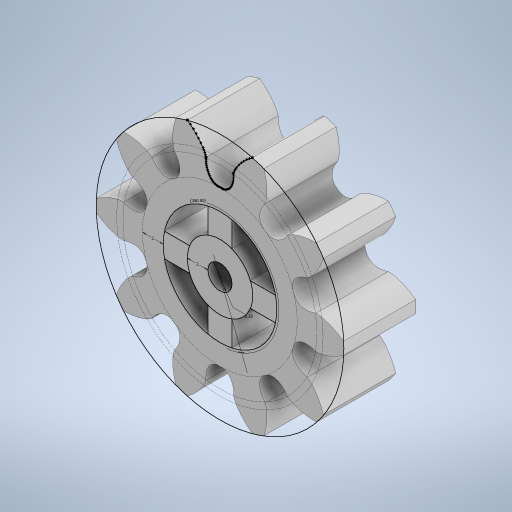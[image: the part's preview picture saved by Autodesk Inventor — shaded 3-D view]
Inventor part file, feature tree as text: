
AUTODESK INVENTOR PART (.ipt)
format: ipt  version: 2023 (Build 270158000, 158)  size: 391,680 bytes
history: native  units: mm
features: extrude x3, sketch x1, pattern_circular x1
ambient origin geometry x8: Origin, YZ Plane, XZ Plane, XY Plane, X Axis, Y Axis, Z Axis, Center Point
bodies: Solid1 (feature_tree)
feature tree (5):
  sketch  "Sketch1"  dims[d0=7.0mm d1=0.0mm d2=2.33mm d3=2.0mm d4=2.0mm d5=40.0mm d7=360.0deg d9=0.0mm d10=0.0mm d11=0.0mm d12=0.0mm d13=100.0mm d14=360.0deg]
  extrude  "Extrusion1"  Depth=2.33mm
  extrude  "Extrusion2"  Depth=2.0mm
  extrude  "Extrusion3"  Depth=2.0mm
  pattern_circular  "Circular Pattern1"  Count=4 Angle=360.0deg
